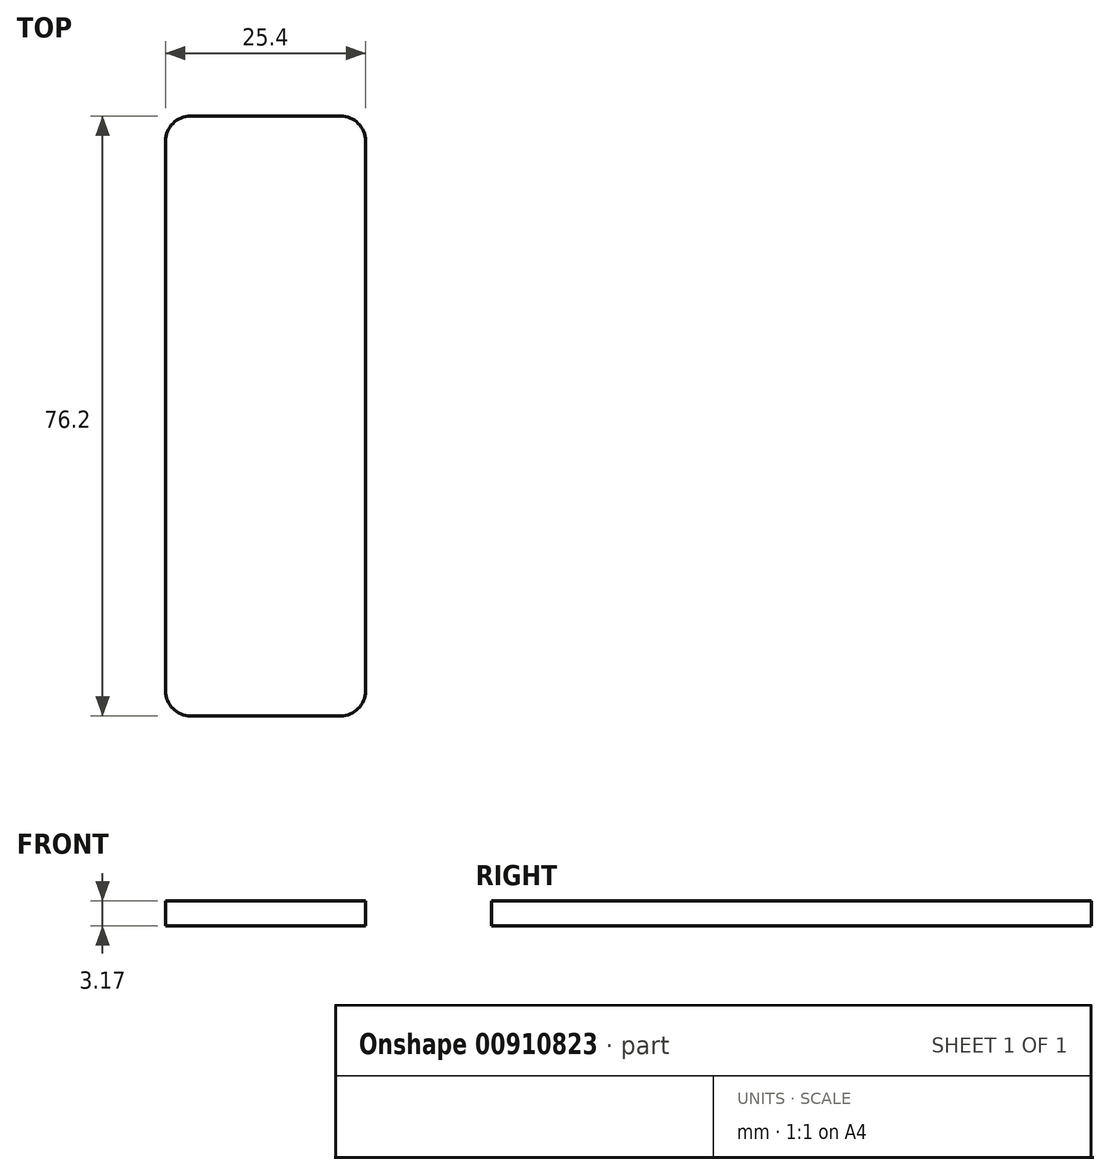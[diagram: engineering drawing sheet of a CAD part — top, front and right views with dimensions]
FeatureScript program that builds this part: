
annotation { "Feature Type Name" : "Feature", "Feature Type Description" : "" }
export const myFeature = defineFeature(function(context is Context, id is Id, definition is map)
    precondition{}
    {
        {
            var Q0;
            Q0=qCreatedBy(makeId("Top.planeOp"),FACE);
            var sketch = newSketch(context, id + "F0", { "sketchPlane" : qUnion([Q0])});
            skLineSegment(sketch, "E0.bottom", {"start": v(3.17, 0) * mm, "end": v(22.23, 0) * mm});
            skLineSegment(sketch, "E0.top", {"start": v(3.17, 76.2) * mm, "end": v(22.22, 76.2) * mm});
            skLineSegment(sketch, "E0.left", {"start": v(0, 3.18) * mm, "end": v(0, 73.03) * mm});
            skLineSegment(sketch, "E0.right", {"start": v(25.4, 3.18) * mm, "end": v(25.4, 73.03) * mm});
            skPoint(sketch, "E1.visualSharp", {"position": v(0, 0) * mm});
            skArc(sketch, "E1.filletArc", {"start": v(0, 3.17) * mm, "mid": v(0.93, 0.93) * mm, "end": v(3.17, 0) * mm});
            skPoint(sketch, "E2.visualSharp", {"position": v(0, 76.2) * mm});
            skArc(sketch, "E2.filletArc", {"start": v(3.17, 76.2) * mm, "mid": v(0.93, 75.27) * mm, "end": v(0, 73.03) * mm});
            skPoint(sketch, "E3.visualSharp", {"position": v(25.4, 0) * mm});
            skArc(sketch, "E3.filletArc", {"start": v(22.23, 0) * mm, "mid": v(24.47, 0.93) * mm, "end": v(25.4, 3.18) * mm});
            skPoint(sketch, "E4.visualSharp", {"position": v(25.4, 76.2) * mm});
            skArc(sketch, "E4.filletArc", {"start": v(25.4, 73.03) * mm, "mid": v(24.47, 75.27) * mm, "end": v(22.22, 76.2) * mm});
            skSolve(sketch);
        }
        {
            var Q0;
            Q0 = qSketchRegion(id + "F0", true);
            extrude(context, id + "F1", {"entities" : qUnion([Q0]), "depth" : 3.17 * mm, "offsetDistance" : 25.4 * mm});
        }
    });
